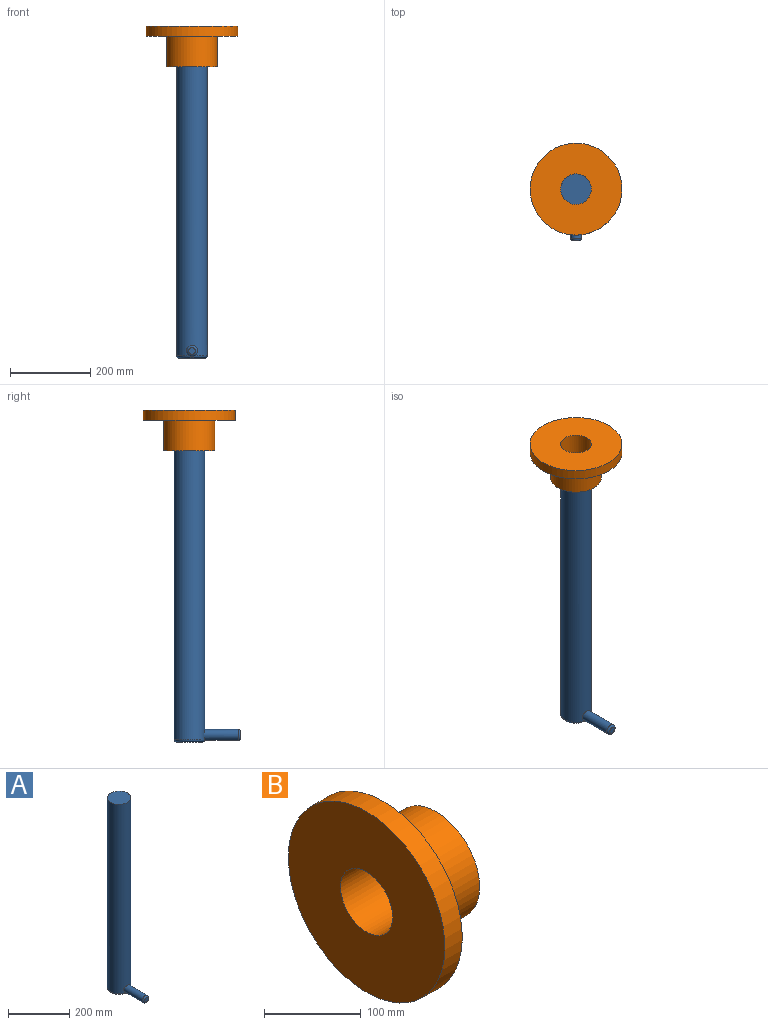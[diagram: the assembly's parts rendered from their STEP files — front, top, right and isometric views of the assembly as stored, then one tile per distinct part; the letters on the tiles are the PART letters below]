
ASSEMBLY  parts=2 mates=1
PART A: 8 faces, bbox 82.5x168.2x762 mm
  f0: cylinder r=38.1mm len=756.92mm, axis (0,0,-1), area 180623.2mm2, adj f1,f3,f6
  f1: plane 76.2x76.2mm, normal (0,0,1), area 4560.4mm2, adj f0
  f2: plane 66.12x66.04mm, normal (0,0,-1), area 3425.7mm2, adj f6,f7
  f3: cylinder r=13.48mm len=86.28mm, axis (0,1,0), area 7203.6mm2, adj f0,f5,f7
  f4: plane 16.8x16.8mm, normal (0,-1,0), area 221.6mm2, adj f5
  f5: torus R=8.4mm, axis (0,-1,0), area 583.2mm2, adj f3,f4
  f6: torus R=33.02mm, axis (0,0,1), area 1744.7mm2, adj f0,f2,f7
  f7: bspline ~11.27x5.5mm, area 67.3mm2, adj f2,f3,f6
PART B: 6 faces, bbox 101.6x228.6x228.6 mm
  f0: cylinder r=38.1mm len=101.6mm, axis (-1,0,0), area 24322mm2, adj f1,f5
  f1: plane 228.6x228.6mm, normal (-1,0,0), area 36482.9mm2, adj f0,f2
  f2: cylinder r=114.3mm len=228.6mm, axis (-1,0,0), area 18241.5mm2, adj f1,f3
  f3: plane 228.6x228.6mm, normal (1,0,0), area 28375.6mm2, adj f2,f4
  f4: cylinder r=63.5mm len=127mm, axis (-1,0,0), area 30402.4mm2, adj f3,f5
  f5: plane 127x127mm, normal (1,0,0), area 8107.3mm2, adj f0,f4
PLACE A t=(76.66,67.67,-3.53)mm
PLACE B rot(axis=(0.71,0,-0.71),180deg) t=(76.66,67.67,821.97)mm
MATE ball B.f0 <-> A.f0  axis (0,0,1) through (76.66,67.67,758.47)mm
